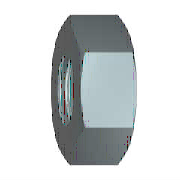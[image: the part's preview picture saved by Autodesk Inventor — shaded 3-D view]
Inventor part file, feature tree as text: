
AUTODESK INVENTOR PART (.ipt)
format: ipt  version: 2019 (Build 230136000, 136)  size: 166,400 bytes
history: native  units: mm (DEFAULTED — no unit token found)
features: sketch x3, chamfer x1, hole x1, other x1, plane x1
ambient origin geometry x7: Origin, YZ Plane, XZ Plane, X Axis, Y Axis, Z Axis, Center Point
bodies: Solid1 (feature_tree), Body (feature_tree)
feature tree (7):
  chamfer  "Chamfer1"  Angle=30.0deg  [1 undecoded]
  hole  "Thread"  [1 undecoded]
  other  "Work Axis1"
  plane  "Work Plane1"
  sketch  "Sketch1"  dims[d0=9.237604mm]
  sketch  "Sketch2"  dims[d1=4.7mm]
  sketch  "Sketch3"  dims[d2=0.0mm d3=30.0deg d4=30.0deg d5=6.9mm d6=6.9mm d7=90.0deg d25=4.134mm d26=6.0mm d27=4.0mm d28=2.0mm d29=14.3117mm d30=8.0mm d31=20.594885mm d8=0.433013mm d9=30.0deg d10=0.433013mm d11=30.0deg d13=0.0mm d14=0.0mm d39=0.0mm d40=0.433013mm d41=0.433013mm d42=0.0mm]
note: 2 required parameter values undecoded (feature->parameter linkage not recoverable at this tier; creation-order binding heuristic only, values carry confidence <= 0.55)
